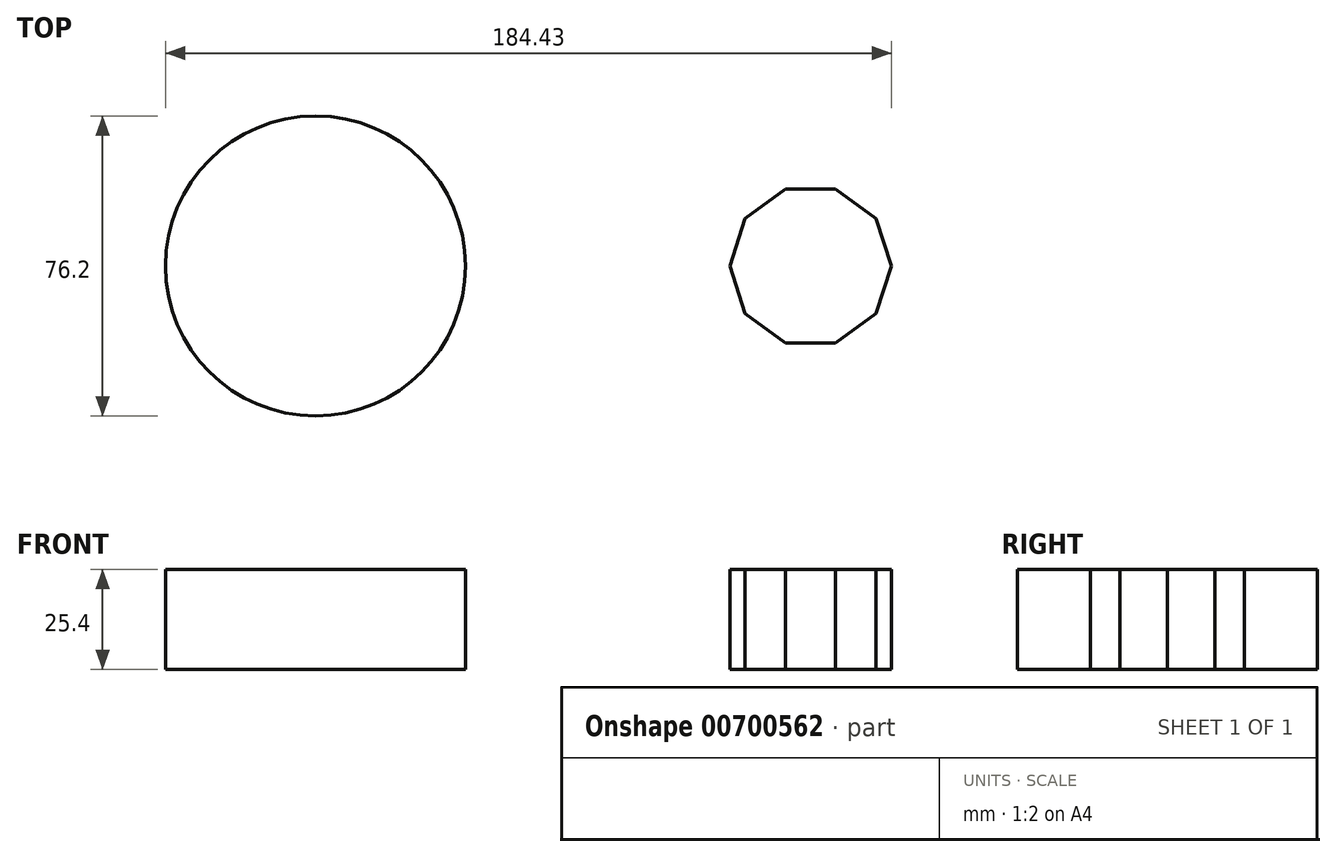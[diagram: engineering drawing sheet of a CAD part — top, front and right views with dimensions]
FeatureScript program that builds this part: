
annotation { "Feature Type Name" : "Feature", "Feature Type Description" : "" }
export const myFeature = defineFeature(function(context is Context, id is Id, definition is map)
    precondition{}
    {
        {
            var Q0;
            Q0=qCreatedBy(makeId("Top.planeOp"),FACE);
            var sketch = newSketch(context, id + "F0", { "sketchPlane" : qUnion([Q0])});
            skCircle(sketch, "E0", {"center": v(0, 0) * mm, "radius": 38.1 * mm});
            skCircle(sketch, "E1.cCircle", {"center": v(125.78, 0) * mm, "radius": 20.55 * mm, "construction": true});
            skLineSegment(sketch, "E1.0", {"start": v(146.33, 0) * mm, "end": v(142.4, -12.08) * mm});
            skLineSegment(sketch, "E1.1", {"start": v(142.4, -12.08) * mm, "end": v(132.13, -19.54) * mm});
            skLineSegment(sketch, "E1.2", {"start": v(132.13, -19.54) * mm, "end": v(119.43, -19.54) * mm});
            skLineSegment(sketch, "E1.3", {"start": v(119.43, -19.54) * mm, "end": v(109.16, -12.08) * mm});
            skLineSegment(sketch, "E1.4", {"start": v(109.16, -12.08) * mm, "end": v(105.23, 0) * mm});
            skLineSegment(sketch, "E1.5", {"start": v(105.23, 0) * mm, "end": v(109.16, 12.08) * mm});
            skLineSegment(sketch, "E1.6", {"start": v(109.16, 12.08) * mm, "end": v(119.43, 19.54) * mm});
            skLineSegment(sketch, "E1.7", {"start": v(119.43, 19.54) * mm, "end": v(132.13, 19.54) * mm});
            skLineSegment(sketch, "E1.8", {"start": v(132.13, 19.54) * mm, "end": v(142.4, 12.08) * mm});
            skLineSegment(sketch, "E1.9", {"start": v(142.4, 12.08) * mm, "end": v(146.33, 0) * mm});
            skLineSegment(sketch, "E2", {"start": v(0, 38.1) * mm, "end": v(125.78, 20.55) * mm});
            skPoint(sketch, "E2.endSnap0", {"position": v(125.78, 19.54) * mm});
            skLineSegment(sketch, "E3", {"start": v(0, -38.1) * mm, "end": v(125.78, -19.54) * mm});
            skSolve(sketch);
        }
        {
            var Q0;
            Q0 = qSketchRegion(id + "F0", true);
            extrude(context, id + "F1", {"entities" : qUnion([Q0]), "endBound" : BoundingType.SYMMETRIC, "depth" : 25.4 * mm, "offsetDistance" : 25.4 * mm});
        }
    });
